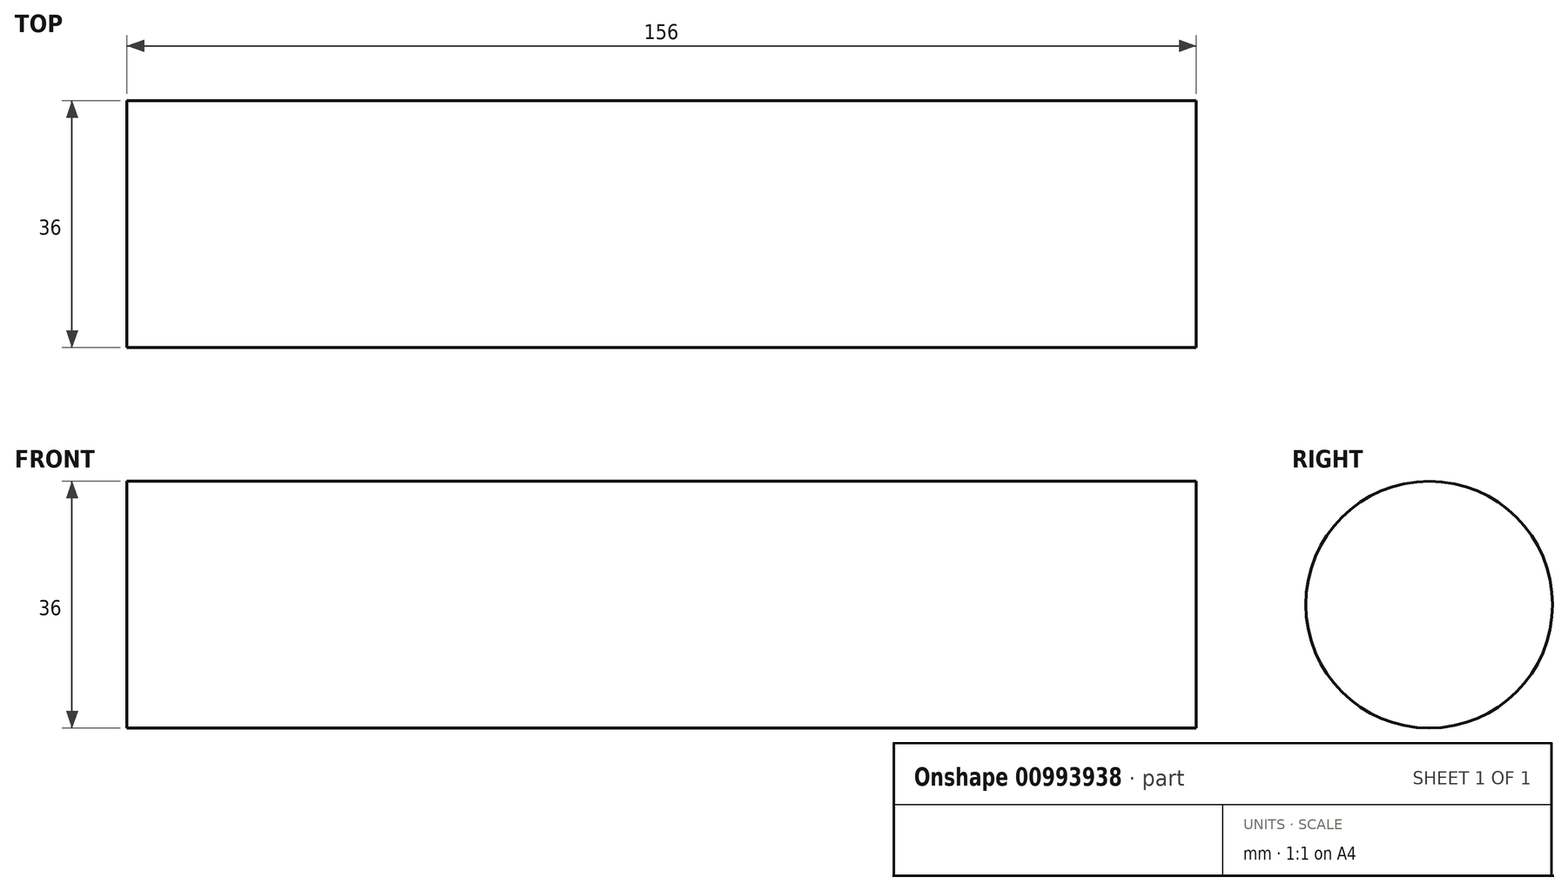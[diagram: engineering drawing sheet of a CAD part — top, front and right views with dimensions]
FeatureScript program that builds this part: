
annotation { "Feature Type Name" : "Feature", "Feature Type Description" : "" }
export const myFeature = defineFeature(function(context is Context, id is Id, definition is map)
    precondition{}
    {
        {
            var Q0;
            Q0=qCreatedBy(makeId("Right.planeOp"),FACE);
            var sketch = newSketch(context, id + "F0", { "sketchPlane" : qUnion([Q0])});
            skCircle(sketch, "E0", {"center": v(0, 0) * mm, "radius": 18 * mm});
            skSolve(sketch);
        }
        {
            var Q0;
            Q0 = qSketchRegion(id + "F0", true);
            extrude(context, id + "F1", {"entities" : qUnion([Q0]), "depth" : 156 * mm, "offsetDistance" : 25 * mm});
        }
    });
